# Revit family: IS_Tesi_Multiproduct_BIM_GB_T3527;T3528
name_source: partatom
category: Plumbing Fixtures
revit_build: Autodesk Revit MEP 2016 (Build: 20161004_0715(x64)
units: mm (PartAtom-declared; Revit-internal decimal feet)

## family parameters
Cut with Voids When Loaded = No
Host = Face
OmniClass Number = 23.45.05.21.11.11
OmniClass Title = Water Operated Water Closets
Part Type = Normal
Room Calculation Point = No
Round Connector Dimension = Use Diameter
Shared = Yes

## types (2) — shared parameters
Accessories = www.idealstandard.de\ersatzteile
AreaUnits = millimeters
Assembly Code = C1030200
AssetType = Fixed
BREEAMApproved = No
Brand = Ideal Standard
ConnectionType = Plumbing
DurationUnit = year
ECA = No
ExpectedLife = 5
Finish = White
Help = www.idealspec.co.uk/contact-us.html
IfcExportAs = IfcSanitaryTerminalType
IfcExportType = SEAT&COVER
InstallationInstructions = www.idealspec.co.uk/resources.html
LinearUnits = millimeters
ManufacturerURL = www.idealspec.co.uk
NBSDescription = WC pans
NBSReference = 45-30-70/384
NettWeight = 2.2 Kg
NominalDepth = 446 mm
NominalHeight = 47 mm
NominalLength = 446 mm
NominalWidth = 367 mm
PanColor = White
PanMaterial = Vitreous china
PanMounting = BackToWall
Shape = Sculptured
Size = 367 x 446 x  47 mm
Space = Internal
ToiletPanType = WashDown
ToiletType = Other
Uniclass2015Description = WC seats and covers
Uniclass2015Reference = Pr_40_20_93_95
Uniclass2015Version = Products v1.1
Version = 1
VolumeUnits = Litres
WRAS = No
WarrantyDescription = Manufacturers Warranty
WarrantyDurationParts = 5
WarrantyDurationUnit = year
WaterEfficientProduct = No
zero-valued in all types: CWFU, Cost, Default Elevation, HWFU, SpilloverLevel, WFU

## per-type parameters (varying)
| type | BIMObjectName | Description | Features | Model | ModelNumber | ModelReference | Name | ProductInformation | URL |
| T352701-Tesi Seat&Cover Soft Close - thin Sandwich | ISI_IdealStandard_WCSeats_Tesi_T3527 | Tesi toilet seat and cover, slow close slim style | Toilet Seat And Cover, Slow Close Slim Style | T352701 | T352701 | Tesi toilet seat and cover, slow close slim style | WCSeats_Tesi_T3527_IdealStandard | www.idealspec.co.uk/assets/datasheet/T352701 | www.idealstandard.de |
| T352801-Tesi Seat&Cover Normal Close - thin Sandwich | ISI_IdealStandard_WCSeats_Tesi_T3528 | Tesi toilet seat and cover, normal close slim style | Toilet Seat And Cover, Normal Close Slim Style | T352801 | T352801 | Tesi toilet seat and cover, normal close slim style | WCSeats_Tesi_T3528_IdealStandard | www.idealspec.co.uk/assets/datasheet/T352801 | www.idealspec.de |

## geometry (parser evidence)
native form markers: Sweep x2
no freeform markers — native parametric forms only
